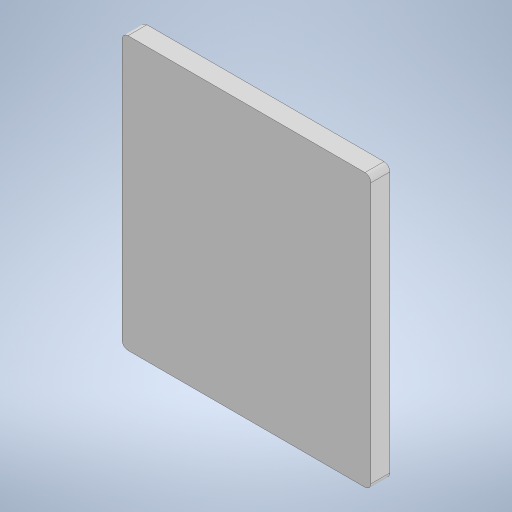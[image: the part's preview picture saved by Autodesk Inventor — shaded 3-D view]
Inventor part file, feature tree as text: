
AUTODESK INVENTOR PART (.ipt)
format: ipt  version: 2024.2 (Build 282272000, 272)  size: 202,240 bytes
history: native  units: mm
features: extrude x1, fillet x1, sketch x1
ambient origin geometry x8: Origin, YZ Plane, XZ Plane, XY Plane, X Axis, Y Axis, Z Axis, Center Point
bodies: Solid1 (feature_tree)
feature tree (3):
  extrude  "Extrusion1"  Depth=23.0mm
  fillet  "Fillet1"  Radius=1.6mm
  sketch  "Sketch1"  dims[d1=21.0mm d2=23.0mm d3=1.6mm d4=0.0mm d5=0.5mm]
